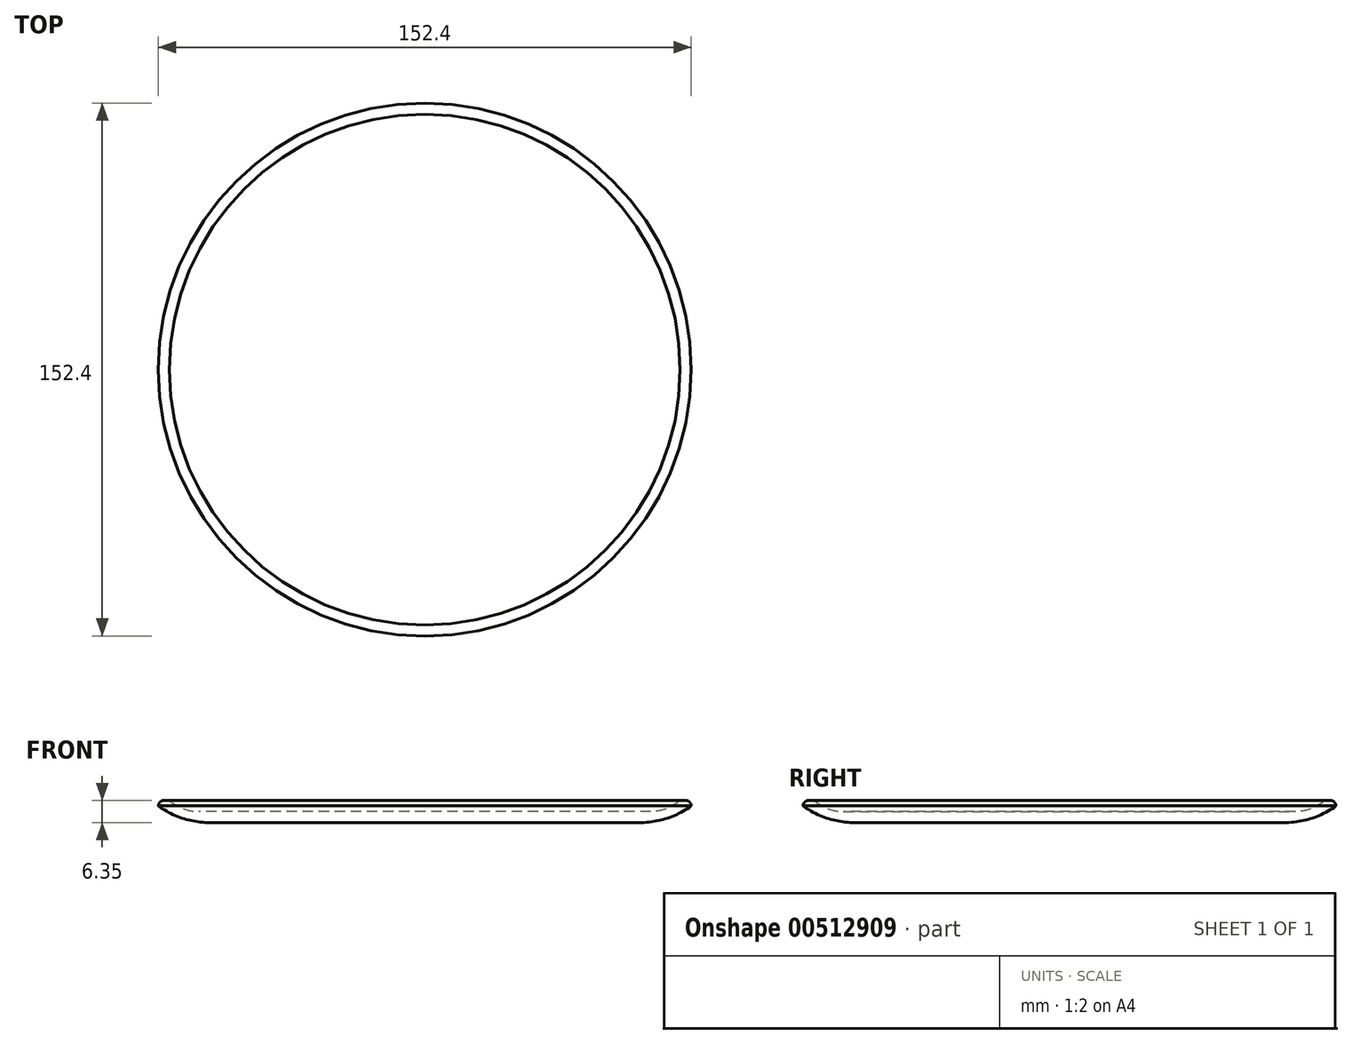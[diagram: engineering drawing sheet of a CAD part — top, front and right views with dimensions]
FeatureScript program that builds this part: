
annotation { "Feature Type Name" : "Feature", "Feature Type Description" : "" }
export const myFeature = defineFeature(function(context is Context, id is Id, definition is map)
    precondition{}
    {
        {
            var Q0;
            Q0=qCreatedBy(makeId("Top.planeOp"),FACE);
            var sketch = newSketch(context, id + "F0", { "sketchPlane" : qUnion([Q0])});
            skCircle(sketch, "E0", {"center": v(0, 0) * mm, "radius": 76.2 * mm});
            skSolve(sketch);
        }
        {
            var Q0;
            Q0=makeQuery(id+"F0.imprint","IMPRINT",FACE,{"disambiguationData":[TD([[makeQuery(id+"F0.imprint","IMPRINT",EDGE,{"derivedFrom":sQuery(id+"F0.wireOp",EDGE,"E0")}),1.0]])]});
            extrude(context, id + "F1", {"entities" : qUnion([Q0]), "depth" : 6.35 * mm});
        }
        {
            var Q0;
            Q0=makeQuery(id+"F1.opExtrude","CAP_FACE",FACE,{"disambiguationData":[OSD([sQuery(id+"F0.wireOp",EDGE,"E0")])],"isStart":false});
            var sketch = newSketch(context, id + "F2", { "sketchPlane" : qUnion([Q0])});
            skCircle(sketch, "E1", {"center": v(0, 0) * mm, "radius": 73.02 * mm});
            skSolve(sketch);
        }
        {
            var Q0;
            Q0=makeQuery(id+"F2.imprint","IMPRINT",FACE,{"disambiguationData":[TD([[makeQuery(id+"F2.imprint","IMPRINT",EDGE,{"derivedFrom":sQuery(id+"F2.wireOp",EDGE,"E1")}),1.0]])]});
            extrude(context, id + "F3", {"entities" : qUnion([Q0]), "operationType" : NewBodyOperationType.REMOVE, "oppositeDirection" : true, "depth" : 3.17 * mm});
        }
        {
            var Q0;
            Q0=makeQuery(id+"F3.boolean.opBoolean","COPY",EDGE,{"derivedFrom":makeQuery(id+"F3.opExtrude","CAP_EDGE",EDGE,{"disambiguationData":[OSD([sQuery(id+"F2.wireOp",EDGE,"E1")])],"isStart":true})});
            var Q1;
            Q1=makeQuery(id+"F1.opExtrude","CAP_EDGE",EDGE,{"disambiguationData":[OSD([sQuery(id+"F0.wireOp",EDGE,"E0")])],"isStart":false});
            fillet(context, id + "F4", {"entities" : qUnion([Q0, Q1]), "radius" : 1.59 * mm, "tangentPropagation" : true, "allowEdgeOverflow" : false});
        }
        {
            var Q0;
            Q0=makeQuery(id+"F3.boolean.opBoolean","COPY",EDGE,{"derivedFrom":makeQuery(id+"F3.opExtrude","CAP_EDGE",EDGE,{"disambiguationData":[OSD([sQuery(id+"F2.wireOp",EDGE,"E1")])],"isStart":false})});
            fillet(context, id + "F5", {"entities" : qUnion([Q0]), "radius" : 12.7 * mm, "tangentPropagation" : true, "allowEdgeOverflow" : false});
        }
        {
            var Q0;
            Q0=makeQuery(id+"F1.opExtrude","CAP_EDGE",EDGE,{"disambiguationData":[OSD([sQuery(id+"F0.wireOp",EDGE,"E0")])],"isStart":true});
            fillet(context, id + "F6", {"entities" : qUnion([Q0]), "radius" : 25.4 * mm, "tangentPropagation" : true, "allowEdgeOverflow" : false});
        }
    });
